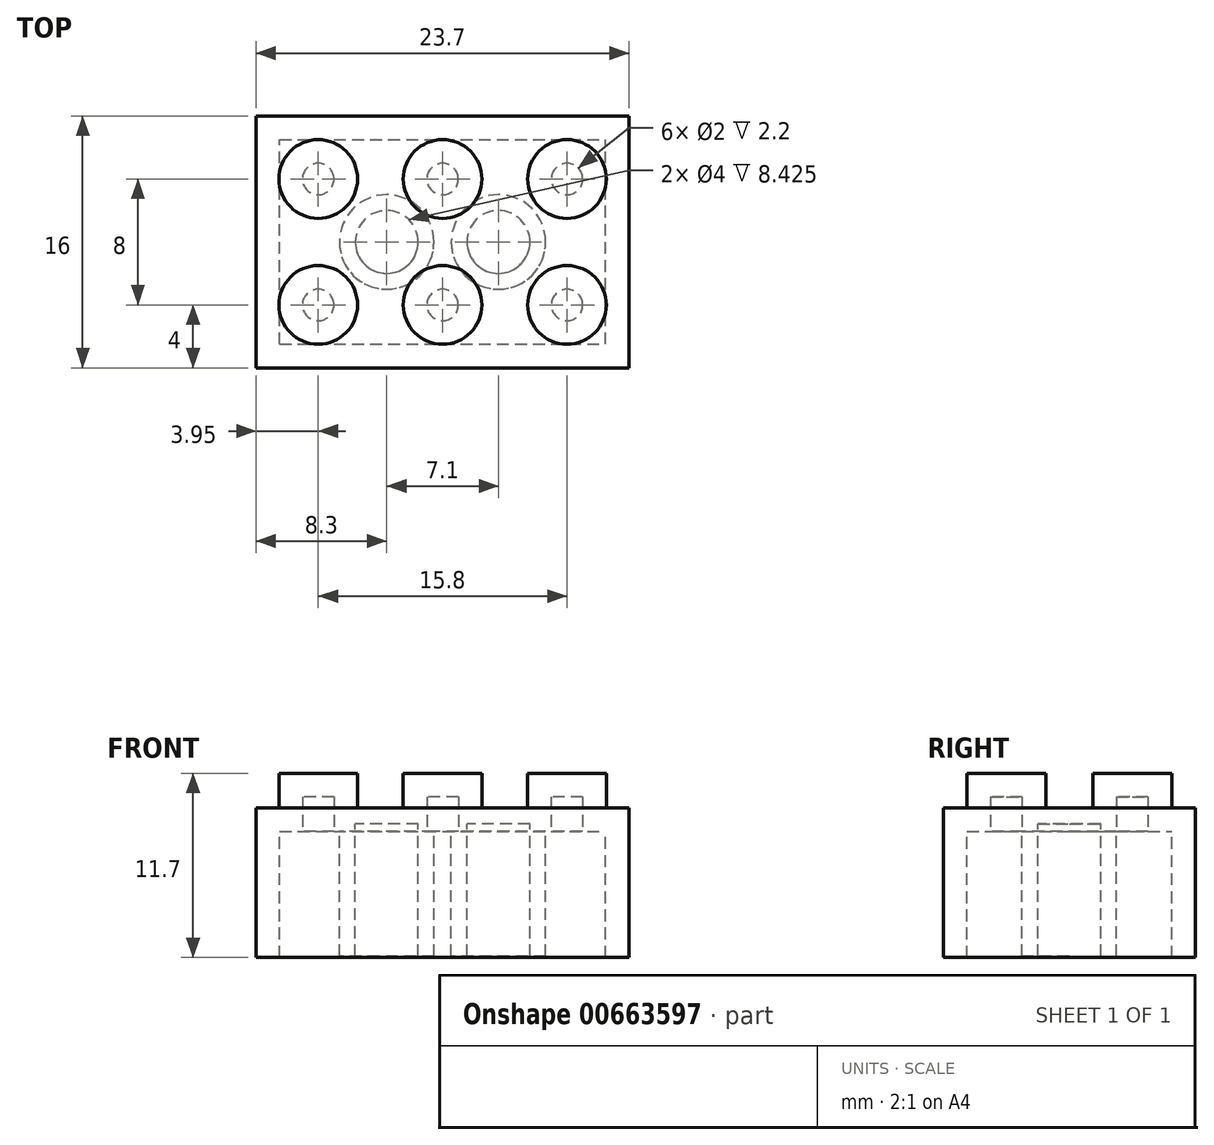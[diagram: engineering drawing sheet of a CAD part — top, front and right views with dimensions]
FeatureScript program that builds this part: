
annotation { "Feature Type Name" : "Feature", "Feature Type Description" : "" }
export const myFeature = defineFeature(function(context is Context, id is Id, definition is map)
    precondition{}
    {
        {
            var Q0;
            Q0=qCreatedBy(makeId("Top.planeOp"),FACE);
            var sketch = newSketch(context, id + "F0", { "sketchPlane" : qUnion([Q0])});
            skLineSegment(sketch, "E0.bottom", {"start": v(0, 0) * mm, "end": v(23.7, 0) * mm});
            skLineSegment(sketch, "E0.top", {"start": v(0, 8) * mm, "end": v(23.7, 8) * mm});
            skLineSegment(sketch, "E0.left", {"start": v(0, 0) * mm, "end": v(0, 8) * mm});
            skLineSegment(sketch, "E0.right", {"start": v(23.7, 0) * mm, "end": v(23.7, 8) * mm});
            skPoint(sketch, "E1", {"position": v(0, 4) * mm});
            skLineSegment(sketch, "E2", {"start": v(0, 4) * mm, "end": v(23.7, 4) * mm, "construction": true});
            skPoint(sketch, "E3", {"position": v(11.85, 8) * mm});
            skLineSegment(sketch, "E4", {"start": v(11.85, 8) * mm, "end": v(11.85, 0) * mm, "construction": true});
            skCircle(sketch, "E5", {"center": v(11.85, 4) * mm, "radius": 2.5 * mm});
            skCircle(sketch, "E6", {"center": v(19.75, 4) * mm, "radius": 2.5 * mm});
            skCircle(sketch, "E7", {"center": v(3.95, 4) * mm, "radius": 2.5 * mm});
            skSolve(sketch);
        }
        {
            var Q0;
            Q0=makeQuery(id+"F0.imprint","IMPRINT",FACE,{"disambiguationData":[TD([[makeQuery(id+"F0.imprint","IMPRINT",EDGE,{"derivedFrom":sQuery(id+"F0.wireOp",EDGE,"E6")}),1.0]])]});
            var Q1;
            Q1=makeQuery(id+"F0.imprint","IMPRINT",FACE,{"disambiguationData":[TD([[makeQuery(id+"F0.imprint","IMPRINT",EDGE,{"derivedFrom":sQuery(id+"F0.wireOp",EDGE,"E5")}),1.0]])]});
            var Q2;
            Q2=makeQuery(id+"F0.imprint","IMPRINT",FACE,{"disambiguationData":[TD([[makeQuery(id+"F0.imprint","IMPRINT",EDGE,{"derivedFrom":sQuery(id+"F0.wireOp",EDGE,"E7")}),1.0]])]});
            var Q3;
            Q3=makeQuery(id+"F0.imprint","IMPRINT",FACE,{"disambiguationData":[TD([[makeQuery(id+"F0.imprint","IMPRINT",EDGE,{"derivedFrom":sQuery(id+"F0.wireOp",EDGE,"E0.bottom")}),1.0]])]});
            extrude(context, id + "F1", {"entities" : qUnion([Q0, Q1, Q2, Q3]), "oppositeDirection" : true, "depth" : 9.5 * mm, "offsetDistance" : 25.4 * mm});
        }
        {
            var Q0;
            Q0=makeQuery(id+"F0.imprint","IMPRINT",FACE,{"disambiguationData":[TD([[makeQuery(id+"F0.imprint","IMPRINT",EDGE,{"derivedFrom":sQuery(id+"F0.wireOp",EDGE,"E7")}),1.0]])]});
            var Q1;
            Q1=makeQuery(id+"F0.imprint","IMPRINT",FACE,{"disambiguationData":[TD([[makeQuery(id+"F0.imprint","IMPRINT",EDGE,{"derivedFrom":sQuery(id+"F0.wireOp",EDGE,"E5")}),1.0]])]});
            var Q2;
            Q2=makeQuery(id+"F0.imprint","IMPRINT",FACE,{"disambiguationData":[TD([[makeQuery(id+"F0.imprint","IMPRINT",EDGE,{"derivedFrom":sQuery(id+"F0.wireOp",EDGE,"E6")}),1.0]])]});
            extrude(context, id + "F2", {"entities" : qUnion([Q0, Q1, Q2]), "operationType" : NewBodyOperationType.ADD, "depth" : 2.2 * mm, "offsetDistance" : 25.4 * mm});
        }
        {
            var Q0;
            Q0=makeQuery(id+"F1.opExtrude","SWEPT_BODY",BODY,{"disambiguationData":[OSD([sQuery(id+"F0.wireOp",EDGE,"E0.bottom"),sQuery(id+"F0.wireOp",EDGE,"E0.top"),sQuery(id+"F0.wireOp",EDGE,"E0.left"),sQuery(id+"F0.wireOp",EDGE,"E0.right")])]});
            var Q1;
            Q1=makeQuery(id+"F1.opExtrude","SWEPT_FACE",FACE,{"disambiguationData":[OSD([sQuery(id+"F0.wireOp",EDGE,"E0.bottom")])]});
            mirror(context, id + "F3", {"operationType" : NewBodyOperationType.ADD, "entities" : qUnion([Q0]), "mirrorPlane" : qUnion([Q1])});
        }
        {
            var Q0;
            {var subQ0=makeQuery(id+"F1.opExtrude","CAP_FACE",FACE,{"disambiguationData":[OSD([sQuery(id+"F0.wireOp",EDGE,"E0.bottom"),sQuery(id+"F0.wireOp",EDGE,"E0.top"),sQuery(id+"F0.wireOp",EDGE,"E0.left"),sQuery(id+"F0.wireOp",EDGE,"E0.right")])],"isStart":false});Q0=makeQuery(id+"F3.boolean.opBoolean","MERGE",FACE,{"derivedFrom":[subQ0,makeQuery(id+"F3.opPattern","COPY",FACE,{"derivedFrom":subQ0,"instanceName":"1"})]});}
            shell(context, id + "F4", {"entities" : qUnion([Q0]), "thickness" : 1.5 * mm});
        }
        {
            var Q0;
            Q0=makeQuery(id+"F4.opShell","OFFSET_FACE",FACE,{"disambiguationData":[OSD([sQuery(id+"F0.wireOp",EDGE,"E0.bottom"),sQuery(id+"F0.wireOp",EDGE,"E0.top"),sQuery(id+"F0.wireOp",EDGE,"E0.left"),sQuery(id+"F0.wireOp",EDGE,"E0.right")])]});
            var sketch = newSketch(context, id + "F5", { "sketchPlane" : qUnion([Q0])});
            skLineSegment(sketch, "E8", {"start": v(22.2, 0) * mm, "end": v(1.5, 0) * mm, "construction": true});
            skCircle(sketch, "E9", {"center": v(8.3, 0) * mm, "radius": 3 * mm});
            skCircle(sketch, "E10", {"center": v(15.4, 0) * mm, "radius": 3 * mm});
            skSolve(sketch);
        }
        {
            var Q0;
            Q0 = qSketchRegion(id + "F5", true);
            extrude(context, id + "F6", {"entities" : qUnion([Q0]), "operationType" : NewBodyOperationType.ADD, "depth" : 7.92 * mm, "offsetDistance" : 25.4 * mm});
        }
        {
            var Q0;
            Q0=makeQuery(id+"F6.opExtrude","CAP_FACE",FACE,{"disambiguationData":[OSD([sQuery(id+"F5.wireOp",EDGE,"E10")])],"isStart":false});
            var Q1;
            Q1=makeQuery(id+"F6.opExtrude","CAP_FACE",FACE,{"disambiguationData":[OSD([sQuery(id+"F5.wireOp",EDGE,"E9")])],"isStart":false});
            shell(context, id + "F7", {"entities" : qUnion([Q0, Q1]), "thickness" : 1 * mm});
        }
    });
